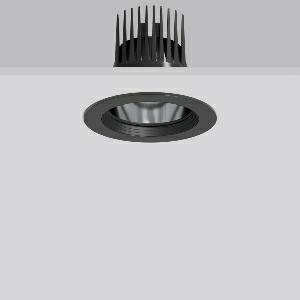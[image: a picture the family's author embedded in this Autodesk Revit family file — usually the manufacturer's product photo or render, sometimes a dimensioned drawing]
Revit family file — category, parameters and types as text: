
# Revit family: heledon_maxi_e_901765_003_ec4d
name_source: partatom
category: Lighting Fixtures
units: mm (PartAtom-declared; Revit-internal decimal feet)

## family parameters
Cut with Voids When Loaded = No
Host = Face
Light Source = No
Part Type = Normal
Room Calculation Point = No
Round Connector Dimension = Use Diameter
Shared = No

## types (1)
- HELEDON maxi E (1 x LED Modul 930, 4350 lm, 3000)
    Apparent Load = 35 VA
    Approval mark = CE
    CIE Flux Codes = 100 100 100 100 100
    Color Rendering = 90
    Color Temperature = 3000
    Default Elevation = 1800 mm
    Description = Series: HELEDON maxi
Round recessed downlight. Housing: die-cast aluminium, powder-coated. Black plastic ring and recessed LED to prevent glare from the side. Optical assembly with reflector made of MIRO-Silver with 98% total light reflection for outstanding efficiency - can be changed without tools. Best colour rendering index Ra>90. Suitable for Recessed ceiling mounting. Installation without tools thanks to spring fastening system. Including separate LED converter with connecting cable 600 mm.High quality converter without flickering and stroboscopic effect. Through-wiring box (5 pole) available as accessory. The following accessories can be mounted without use of tools: interchangeable lenses, decorative glasses, honeycomb louvre, clear and frosted diffusers, white interchangeable plastic ring. 
Colour: deep black, matt (RAL 9005)
Diameter: 162 mm
Height: 3 mm
Cut-out diameter: 152 mm
Recess height: 200 mm
Luminaire: recess height: 135 mm
Lamp: LED
Socket: without socket
Colour temperature: 3000K
Colour rendering index (CRI): 92
System power: 35 W
Rated luminous flux: 4350 lm
Luminous efficiency: 124 lm/W
Control gear: Regulated power supply
Protection class: II
Type of protection: IP 20
    Height = 0 mm  [stored 0 ft]
    Lamp = 1 x LED Modul 930
    Lamp Light Flux = 4350 lm
    Lamp count = 1
    Length = 162 mm
    Lifetime = 50000 h
    Luminous efficacy = 124 lm/W
    Manufacturer = RZB
    ModVariant = No
    Model = 901765.003
    Mounting Place = Ceiling
    Mounting Type = Recessed
    Number of Poles = 1
    OnlyDefault = Yes
    Power Factor = 1
    Product Name = HELEDON maxi E
    Product group = Recessed downlights
    ProductGroupID = 402
    Protection Class = Protection class II
    Protection Degree = IP 20
    RLX_Detail_Level = 1
    RLX_Emergency_Light_Flux = 0 lm
    RLX_Emergency_Type = 0
    RLX_Emergency_Type_DB = No
    RlxData = <blob elided: 121753 chars, md5=268be04f>
    Socket = socket
    Standby Power = 0 W
    System Light Flux = 4350 lm
    System Power = 35 W
    Type Comments = Product without accessories
    Type Image = 901662.003.jpg
    URL = http://relux.com
    VarID = ---
    Voltage = 230 V
    Voltage Range = 220-240 V
    Weight = 0.00 kg
    Width = 0 mm  [stored 0 ft]

note: [stored X ft] marks values corroborated as IEEE doubles in the binary element streams (Revit-internal decimal feet)

## geometry (parser evidence)
native form markers: Blend x4, Sweep x11
no freeform markers — native parametric forms only
